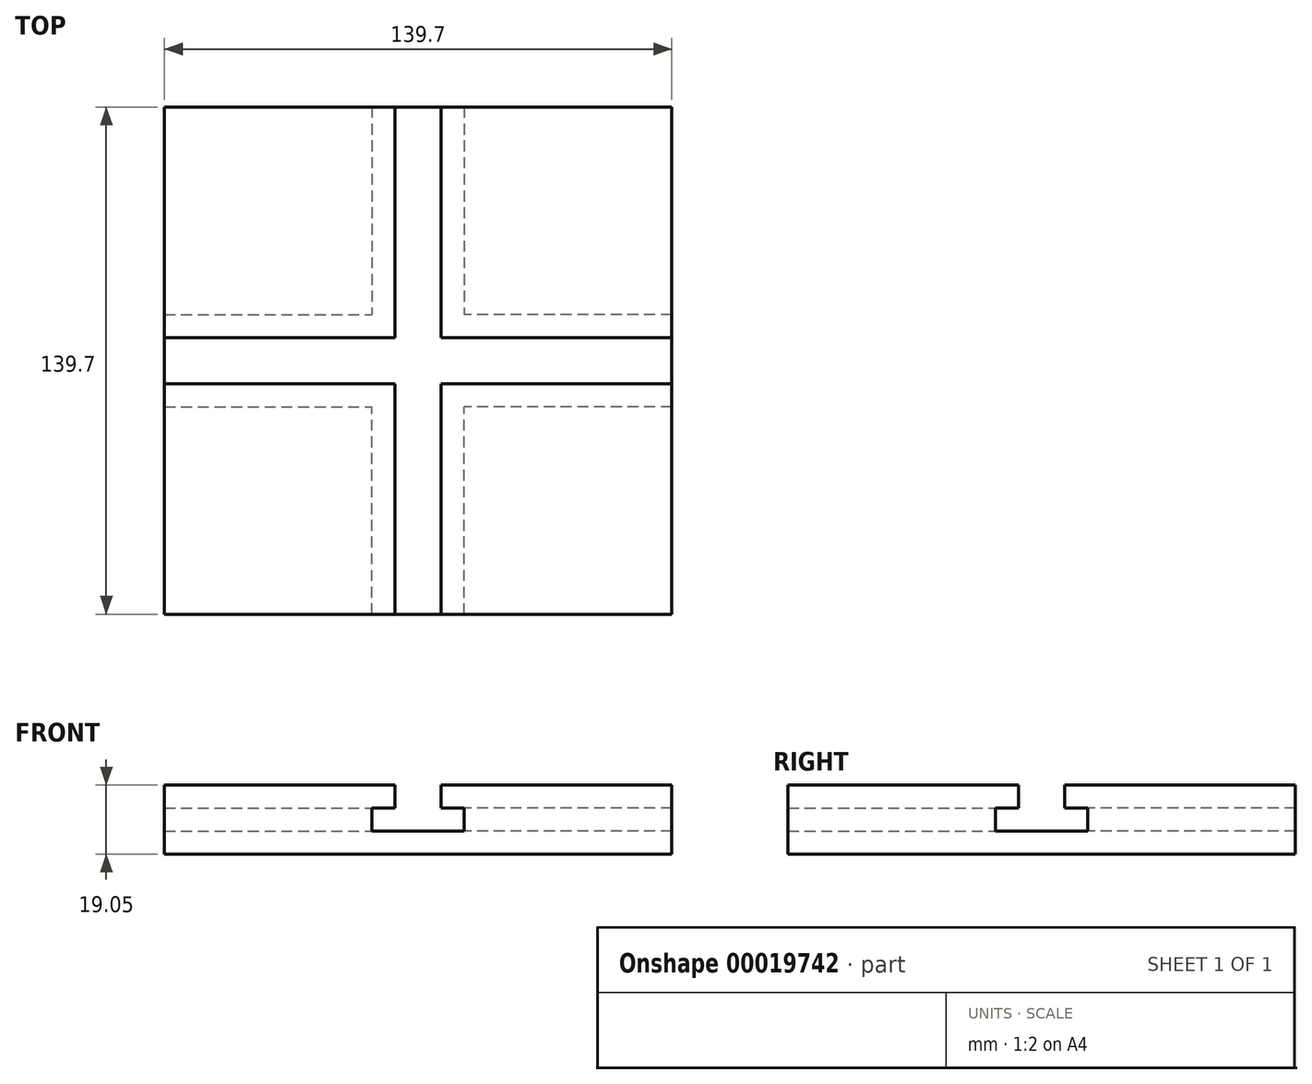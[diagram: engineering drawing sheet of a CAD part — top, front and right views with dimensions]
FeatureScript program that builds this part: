
annotation { "Feature Type Name" : "Feature", "Feature Type Description" : "" }
export const myFeature = defineFeature(function(context is Context, id is Id, definition is map)
    precondition{}
    {
        {
            var Q0;
            Q0=qCreatedBy(makeId("Top.planeOp"),FACE);
            var sketch = newSketch(context, id + "F0", { "sketchPlane" : qUnion([Q0])});
            skLineSegment(sketch, "E0.bottom", {"start": v(0, 0) * mm, "end": v(139.7, 0) * mm});
            skLineSegment(sketch, "E0.top", {"start": v(0, 139.7) * mm, "end": v(139.7, 139.7) * mm});
            skLineSegment(sketch, "E0.left", {"start": v(0, 0) * mm, "end": v(0, 139.7) * mm});
            skLineSegment(sketch, "E0.right", {"start": v(139.7, 0) * mm, "end": v(139.7, 139.7) * mm});
            skSolve(sketch);
        }
        {
            var Q0;
            Q0=qSketchRegion(id+"F0",true);
            extrude(context, id + "F1", {"entities" : qUnion([Q0]), "depth" : 6.35 * mm});
        }
        {
            var Q0;
            Q0=makeQuery(id+"F1.opExtrude","CAP_FACE",FACE,{"disambiguationData":[OSD([sQuery(id+"F0.wireOp",EDGE,"E0.bottom"),sQuery(id+"F0.wireOp",EDGE,"E0.top"),sQuery(id+"F0.wireOp",EDGE,"E0.left"),sQuery(id+"F0.wireOp",EDGE,"E0.right")])],"isStart":false});
            var sketch = newSketch(context, id + "F2", { "sketchPlane" : qUnion([Q0])});
            skLineSegment(sketch, "E1.bottom", {"start": v(0, 139.7) * mm, "end": v(57.15, 139.7) * mm});
            skLineSegment(sketch, "E1.top", {"start": v(0, 82.55) * mm, "end": v(57.15, 82.55) * mm});
            skLineSegment(sketch, "E1.left", {"start": v(0, 139.7) * mm, "end": v(0, 82.55) * mm});
            skLineSegment(sketch, "E1.right", {"start": v(57.15, 139.7) * mm, "end": v(57.15, 82.55) * mm});
            skLineSegment(sketch, "E2.bottom", {"start": v(0, 0) * mm, "end": v(57.15, 0) * mm});
            skLineSegment(sketch, "E2.top", {"start": v(0, 57.15) * mm, "end": v(57.15, 57.15) * mm});
            skLineSegment(sketch, "E2.left", {"start": v(0, 0) * mm, "end": v(0, 57.15) * mm});
            skLineSegment(sketch, "E2.right", {"start": v(57.15, 0) * mm, "end": v(57.15, 57.15) * mm});
            skLineSegment(sketch, "E3.bottom", {"start": v(139.7, 139.7) * mm, "end": v(82.55, 139.7) * mm});
            skLineSegment(sketch, "E3.top", {"start": v(139.7, 82.55) * mm, "end": v(82.55, 82.55) * mm});
            skLineSegment(sketch, "E3.left", {"start": v(139.7, 139.7) * mm, "end": v(139.7, 82.55) * mm});
            skLineSegment(sketch, "E3.right", {"start": v(82.55, 139.7) * mm, "end": v(82.55, 82.55) * mm});
            skLineSegment(sketch, "E4.bottom", {"start": v(139.7, 0) * mm, "end": v(82.55, 0) * mm});
            skLineSegment(sketch, "E4.top", {"start": v(139.7, 57.15) * mm, "end": v(82.55, 57.15) * mm});
            skLineSegment(sketch, "E4.left", {"start": v(139.7, 0) * mm, "end": v(139.7, 57.15) * mm});
            skLineSegment(sketch, "E4.right", {"start": v(82.55, 0) * mm, "end": v(82.55, 57.15) * mm});
            skSolve(sketch);
        }
        {
            var Q0;
            Q0=qSketchRegion(id+"F2",true);
            extrude(context, id + "F3", {"entities" : qUnion([Q0]), "operationType" : NewBodyOperationType.ADD, "depth" : 6.35 * mm});
        }
        {
            var Q0;
            Q0=makeQuery(id+"F3.opExtrude","CAP_FACE",FACE,{"disambiguationData":[OSD([sQuery(id+"F2.wireOp",EDGE,"E2.bottom"),sQuery(id+"F2.wireOp",EDGE,"E2.top"),sQuery(id+"F2.wireOp",EDGE,"E2.left"),sQuery(id+"F2.wireOp",EDGE,"E2.right")])],"isStart":false});
            var sketch = newSketch(context, id + "F4", { "sketchPlane" : qUnion([Q0])});
            skLineSegment(sketch, "E5.bottom", {"start": v(0, 0) * mm, "end": v(63.5, 0) * mm});
            skLineSegment(sketch, "E5.top", {"start": v(0, 63.5) * mm, "end": v(63.5, 63.5) * mm});
            skLineSegment(sketch, "E5.left", {"start": v(0, 0) * mm, "end": v(0, 63.5) * mm});
            skLineSegment(sketch, "E5.right", {"start": v(63.5, 0) * mm, "end": v(63.5, 63.5) * mm});
            skLineSegment(sketch, "E6.bottom", {"start": v(139.7, 0) * mm, "end": v(76.2, 0) * mm});
            skLineSegment(sketch, "E6.top", {"start": v(139.7, 63.5) * mm, "end": v(76.2, 63.5) * mm});
            skLineSegment(sketch, "E6.left", {"start": v(139.7, 0) * mm, "end": v(139.7, 63.5) * mm});
            skLineSegment(sketch, "E6.right", {"start": v(76.2, 0) * mm, "end": v(76.2, 63.5) * mm});
            skLineSegment(sketch, "E7.bottom", {"start": v(139.7, 139.7) * mm, "end": v(76.2, 139.7) * mm});
            skLineSegment(sketch, "E7.top", {"start": v(139.7, 76.2) * mm, "end": v(76.2, 76.2) * mm});
            skLineSegment(sketch, "E7.left", {"start": v(139.7, 139.7) * mm, "end": v(139.7, 76.2) * mm});
            skLineSegment(sketch, "E7.right", {"start": v(76.2, 139.7) * mm, "end": v(76.2, 76.2) * mm});
            skLineSegment(sketch, "E8.bottom", {"start": v(0, 139.7) * mm, "end": v(63.5, 139.7) * mm});
            skLineSegment(sketch, "E8.top", {"start": v(0, 76.2) * mm, "end": v(63.5, 76.2) * mm});
            skLineSegment(sketch, "E8.left", {"start": v(0, 139.7) * mm, "end": v(0, 76.2) * mm});
            skLineSegment(sketch, "E8.right", {"start": v(63.5, 139.7) * mm, "end": v(63.5, 76.2) * mm});
            skSolve(sketch);
        }
        {
            var Q0;
            Q0=qSketchRegion(id+"F4",true);
            extrude(context, id + "F5", {"entities" : qUnion([Q0]), "operationType" : NewBodyOperationType.ADD, "depth" : 6.35 * mm});
        }
    });
